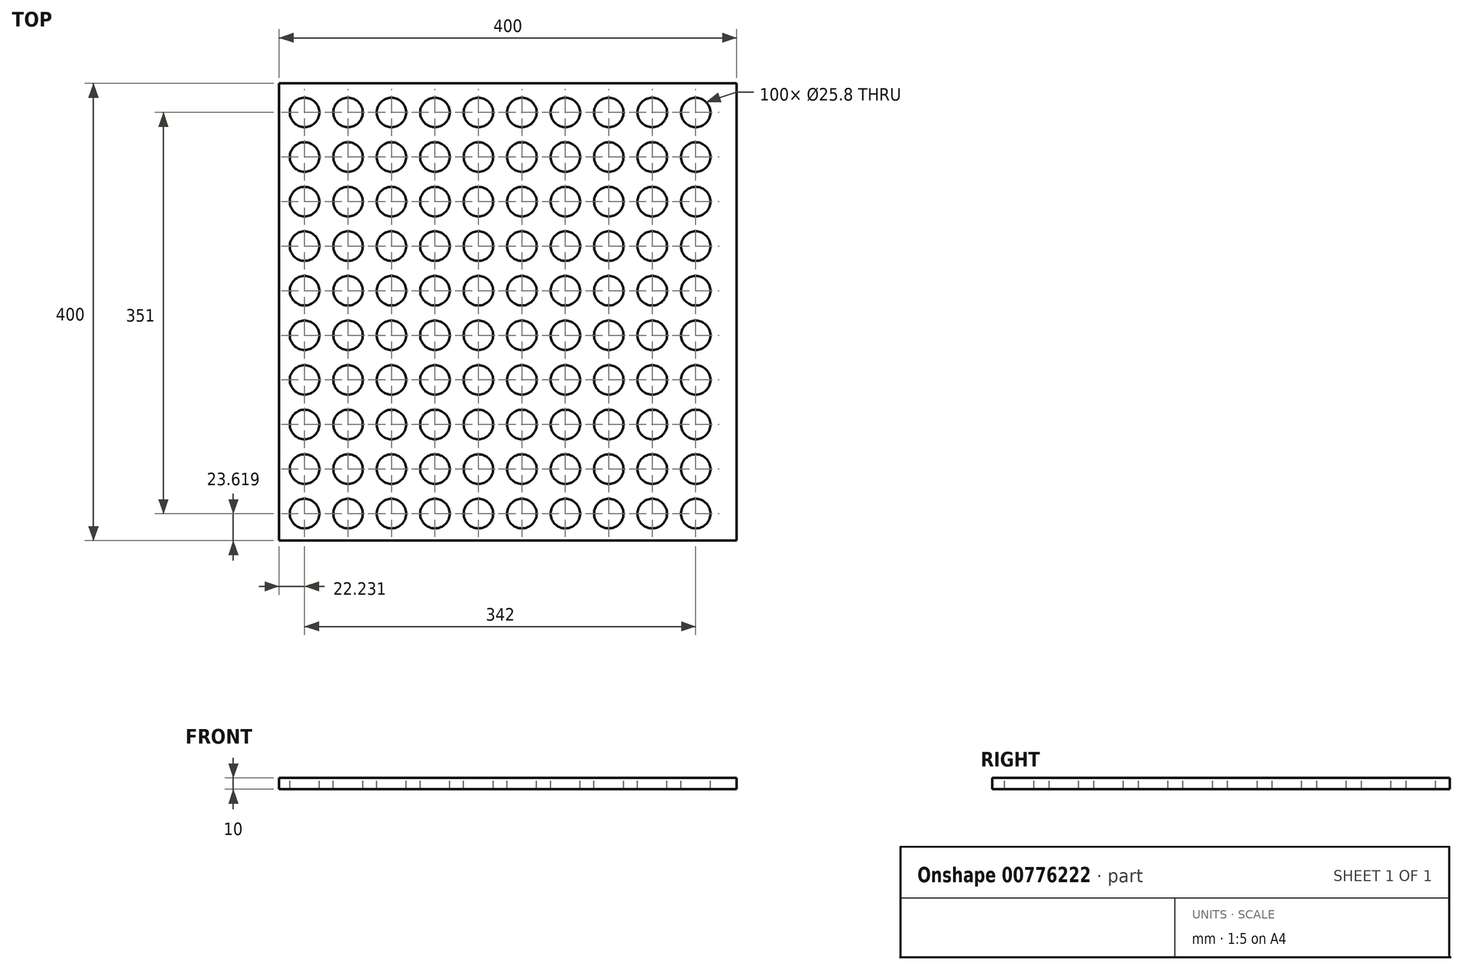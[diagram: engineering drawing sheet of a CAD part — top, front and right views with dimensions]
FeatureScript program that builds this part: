
annotation { "Feature Type Name" : "Feature", "Feature Type Description" : "" }
export const myFeature = defineFeature(function(context is Context, id is Id, definition is map)
    precondition{}
    {
        {
            var Q0;
            Q0=qCreatedBy(makeId("Top.planeOp"),FACE);
            var sketch = newSketch(context, id + "F0", { "sketchPlane" : qUnion([Q0])});
            skLineSegment(sketch, "E0.bottom", {"start": v(-200, 200) * mm, "end": v(200, 200) * mm});
            skLineSegment(sketch, "E0.top", {"start": v(-200, -200) * mm, "end": v(200, -200) * mm});
            skLineSegment(sketch, "E0.left", {"start": v(-200, 200) * mm, "end": v(-200, -200) * mm});
            skLineSegment(sketch, "E0.right", {"start": v(200, 200) * mm, "end": v(200, -200) * mm});
            skPoint(sketch, "E0.middle", {"position": v(0, 0) * mm});
            skSolve(sketch);
        }
        {
            var Q0;
            Q0=qSketchRegion(id+"F0",true);
            extrude(context, id + "F1", {"entities" : qUnion([Q0]), "depth" : 10 * mm, "offsetDistance" : 25 * mm});
        }
        {
            var Q0;
            Q0=makeQuery(id+"F1.opExtrude","CAP_FACE",FACE,{"disambiguationData":[OSD([sQuery(id+"F0.wireOp",EDGE,"E0.bottom"),sQuery(id+"F0.wireOp",EDGE,"E0.top"),sQuery(id+"F0.wireOp",EDGE,"E0.left"),sQuery(id+"F0.wireOp",EDGE,"E0.right")])],"isStart":false});
            var sketch = newSketch(context, id + "F2", { "sketchPlane" : qUnion([Q0])});
            skCircle(sketch, "E1", {"center": v(164.23, -176.38) * mm, "radius": 12.9 * mm});
            skCircle(sketch, "E2.0.1.0", {"center": v(164.23, -137.38) * mm, "radius": 12.9 * mm});
            skCircle(sketch, "E2.0.2.0", {"center": v(164.23, -98.38) * mm, "radius": 12.9 * mm});
            skCircle(sketch, "E2.0.3.0", {"center": v(164.23, -59.38) * mm, "radius": 12.9 * mm});
            skCircle(sketch, "E2.0.4.0", {"center": v(164.23, -20.38) * mm, "radius": 12.9 * mm});
            skCircle(sketch, "E2.0.5.0", {"center": v(164.23, 18.62) * mm, "radius": 12.9 * mm});
            skCircle(sketch, "E2.0.6.0", {"center": v(164.23, 57.62) * mm, "radius": 12.9 * mm});
            skCircle(sketch, "E2.0.7.0", {"center": v(164.23, 96.62) * mm, "radius": 12.9 * mm});
            skCircle(sketch, "E2.0.8.0", {"center": v(164.23, 135.62) * mm, "radius": 12.9 * mm});
            skCircle(sketch, "E2.0.9.0", {"center": v(164.23, 174.62) * mm, "radius": 12.9 * mm});
            skCircle(sketch, "E2.1.0.0", {"center": v(126.23, -176.38) * mm, "radius": 12.9 * mm});
            skCircle(sketch, "E2.1.1.0", {"center": v(126.23, -137.38) * mm, "radius": 12.9 * mm});
            skCircle(sketch, "E2.1.2.0", {"center": v(126.23, -98.38) * mm, "radius": 12.9 * mm});
            skCircle(sketch, "E2.1.3.0", {"center": v(126.23, -59.38) * mm, "radius": 12.9 * mm});
            skCircle(sketch, "E2.1.4.0", {"center": v(126.23, -20.38) * mm, "radius": 12.9 * mm});
            skCircle(sketch, "E2.1.5.0", {"center": v(126.23, 18.62) * mm, "radius": 12.9 * mm});
            skCircle(sketch, "E2.1.6.0", {"center": v(126.23, 57.62) * mm, "radius": 12.9 * mm});
            skCircle(sketch, "E2.1.7.0", {"center": v(126.23, 96.62) * mm, "radius": 12.9 * mm});
            skCircle(sketch, "E2.1.8.0", {"center": v(126.23, 135.62) * mm, "radius": 12.9 * mm});
            skCircle(sketch, "E2.1.9.0", {"center": v(126.23, 174.62) * mm, "radius": 12.9 * mm});
            skCircle(sketch, "E2.2.0.0", {"center": v(88.23, -176.38) * mm, "radius": 12.9 * mm});
            skCircle(sketch, "E2.2.1.0", {"center": v(88.23, -137.38) * mm, "radius": 12.9 * mm});
            skCircle(sketch, "E2.2.2.0", {"center": v(88.23, -98.38) * mm, "radius": 12.9 * mm});
            skCircle(sketch, "E2.2.3.0", {"center": v(88.23, -59.38) * mm, "radius": 12.9 * mm});
            skCircle(sketch, "E2.2.4.0", {"center": v(88.23, -20.38) * mm, "radius": 12.9 * mm});
            skCircle(sketch, "E2.2.5.0", {"center": v(88.23, 18.62) * mm, "radius": 12.9 * mm});
            skCircle(sketch, "E2.2.6.0", {"center": v(88.23, 57.62) * mm, "radius": 12.9 * mm});
            skCircle(sketch, "E2.2.7.0", {"center": v(88.23, 96.62) * mm, "radius": 12.9 * mm});
            skCircle(sketch, "E2.2.8.0", {"center": v(88.23, 135.62) * mm, "radius": 12.9 * mm});
            skCircle(sketch, "E2.2.9.0", {"center": v(88.23, 174.62) * mm, "radius": 12.9 * mm});
            skCircle(sketch, "E2.3.0.0", {"center": v(50.23, -176.38) * mm, "radius": 12.9 * mm});
            skCircle(sketch, "E2.3.1.0", {"center": v(50.23, -137.38) * mm, "radius": 12.9 * mm});
            skCircle(sketch, "E2.3.2.0", {"center": v(50.23, -98.38) * mm, "radius": 12.9 * mm});
            skCircle(sketch, "E2.3.3.0", {"center": v(50.23, -59.38) * mm, "radius": 12.9 * mm});
            skCircle(sketch, "E2.3.4.0", {"center": v(50.23, -20.38) * mm, "radius": 12.9 * mm});
            skCircle(sketch, "E2.3.5.0", {"center": v(50.23, 18.62) * mm, "radius": 12.9 * mm});
            skCircle(sketch, "E2.3.6.0", {"center": v(50.23, 57.62) * mm, "radius": 12.9 * mm});
            skCircle(sketch, "E2.3.7.0", {"center": v(50.23, 96.62) * mm, "radius": 12.9 * mm});
            skCircle(sketch, "E2.3.8.0", {"center": v(50.23, 135.62) * mm, "radius": 12.9 * mm});
            skCircle(sketch, "E2.3.9.0", {"center": v(50.23, 174.62) * mm, "radius": 12.9 * mm});
            skCircle(sketch, "E2.4.0.0", {"center": v(12.23, -176.38) * mm, "radius": 12.9 * mm});
            skCircle(sketch, "E2.4.1.0", {"center": v(12.23, -137.38) * mm, "radius": 12.9 * mm});
            skCircle(sketch, "E2.4.2.0", {"center": v(12.23, -98.38) * mm, "radius": 12.9 * mm});
            skCircle(sketch, "E2.4.3.0", {"center": v(12.23, -59.38) * mm, "radius": 12.9 * mm});
            skCircle(sketch, "E2.4.4.0", {"center": v(12.23, -20.38) * mm, "radius": 12.9 * mm});
            skCircle(sketch, "E2.4.5.0", {"center": v(12.23, 18.62) * mm, "radius": 12.9 * mm});
            skCircle(sketch, "E2.4.6.0", {"center": v(12.23, 57.62) * mm, "radius": 12.9 * mm});
            skCircle(sketch, "E2.4.7.0", {"center": v(12.23, 96.62) * mm, "radius": 12.9 * mm});
            skCircle(sketch, "E2.4.8.0", {"center": v(12.23, 135.62) * mm, "radius": 12.9 * mm});
            skCircle(sketch, "E2.4.9.0", {"center": v(12.23, 174.62) * mm, "radius": 12.9 * mm});
            skCircle(sketch, "E2.5.0.0", {"center": v(-25.77, -176.38) * mm, "radius": 12.9 * mm});
            skCircle(sketch, "E2.5.1.0", {"center": v(-25.77, -137.38) * mm, "radius": 12.9 * mm});
            skCircle(sketch, "E2.5.2.0", {"center": v(-25.77, -98.38) * mm, "radius": 12.9 * mm});
            skCircle(sketch, "E2.5.3.0", {"center": v(-25.77, -59.38) * mm, "radius": 12.9 * mm});
            skCircle(sketch, "E2.5.4.0", {"center": v(-25.77, -20.38) * mm, "radius": 12.9 * mm});
            skCircle(sketch, "E2.5.5.0", {"center": v(-25.77, 18.62) * mm, "radius": 12.9 * mm});
            skCircle(sketch, "E2.5.6.0", {"center": v(-25.77, 57.62) * mm, "radius": 12.9 * mm});
            skCircle(sketch, "E2.5.7.0", {"center": v(-25.77, 96.62) * mm, "radius": 12.9 * mm});
            skCircle(sketch, "E2.5.8.0", {"center": v(-25.77, 135.62) * mm, "radius": 12.9 * mm});
            skCircle(sketch, "E2.5.9.0", {"center": v(-25.77, 174.62) * mm, "radius": 12.9 * mm});
            skCircle(sketch, "E2.6.0.0", {"center": v(-63.77, -176.38) * mm, "radius": 12.9 * mm});
            skCircle(sketch, "E2.6.1.0", {"center": v(-63.77, -137.38) * mm, "radius": 12.9 * mm});
            skCircle(sketch, "E2.6.2.0", {"center": v(-63.77, -98.38) * mm, "radius": 12.9 * mm});
            skCircle(sketch, "E2.6.3.0", {"center": v(-63.77, -59.38) * mm, "radius": 12.9 * mm});
            skCircle(sketch, "E2.6.4.0", {"center": v(-63.77, -20.38) * mm, "radius": 12.9 * mm});
            skCircle(sketch, "E2.6.5.0", {"center": v(-63.77, 18.62) * mm, "radius": 12.9 * mm});
            skCircle(sketch, "E2.6.6.0", {"center": v(-63.77, 57.62) * mm, "radius": 12.9 * mm});
            skCircle(sketch, "E2.6.7.0", {"center": v(-63.77, 96.62) * mm, "radius": 12.9 * mm});
            skCircle(sketch, "E2.6.8.0", {"center": v(-63.77, 135.62) * mm, "radius": 12.9 * mm});
            skCircle(sketch, "E2.6.9.0", {"center": v(-63.77, 174.62) * mm, "radius": 12.9 * mm});
            skCircle(sketch, "E2.7.0.0", {"center": v(-101.77, -176.38) * mm, "radius": 12.9 * mm});
            skCircle(sketch, "E2.7.1.0", {"center": v(-101.77, -137.38) * mm, "radius": 12.9 * mm});
            skCircle(sketch, "E2.7.2.0", {"center": v(-101.77, -98.38) * mm, "radius": 12.9 * mm});
            skCircle(sketch, "E2.7.3.0", {"center": v(-101.77, -59.38) * mm, "radius": 12.9 * mm});
            skCircle(sketch, "E2.7.4.0", {"center": v(-101.77, -20.38) * mm, "radius": 12.9 * mm});
            skCircle(sketch, "E2.7.5.0", {"center": v(-101.77, 18.62) * mm, "radius": 12.9 * mm});
            skCircle(sketch, "E2.7.6.0", {"center": v(-101.77, 57.62) * mm, "radius": 12.9 * mm});
            skCircle(sketch, "E2.7.7.0", {"center": v(-101.77, 96.62) * mm, "radius": 12.9 * mm});
            skCircle(sketch, "E2.7.8.0", {"center": v(-101.77, 135.62) * mm, "radius": 12.9 * mm});
            skCircle(sketch, "E2.7.9.0", {"center": v(-101.77, 174.62) * mm, "radius": 12.9 * mm});
            skCircle(sketch, "E2.8.0.0", {"center": v(-139.77, -176.38) * mm, "radius": 12.9 * mm});
            skCircle(sketch, "E2.8.1.0", {"center": v(-139.77, -137.38) * mm, "radius": 12.9 * mm});
            skCircle(sketch, "E2.8.2.0", {"center": v(-139.77, -98.38) * mm, "radius": 12.9 * mm});
            skCircle(sketch, "E2.8.3.0", {"center": v(-139.77, -59.38) * mm, "radius": 12.9 * mm});
            skCircle(sketch, "E2.8.4.0", {"center": v(-139.77, -20.38) * mm, "radius": 12.9 * mm});
            skCircle(sketch, "E2.8.5.0", {"center": v(-139.77, 18.62) * mm, "radius": 12.9 * mm});
            skCircle(sketch, "E2.8.6.0", {"center": v(-139.77, 57.62) * mm, "radius": 12.9 * mm});
            skCircle(sketch, "E2.8.7.0", {"center": v(-139.77, 96.62) * mm, "radius": 12.9 * mm});
            skCircle(sketch, "E2.8.8.0", {"center": v(-139.77, 135.62) * mm, "radius": 12.9 * mm});
            skCircle(sketch, "E2.8.9.0", {"center": v(-139.77, 174.62) * mm, "radius": 12.9 * mm});
            skCircle(sketch, "E2.9.0.0", {"center": v(-177.77, -176.38) * mm, "radius": 12.9 * mm});
            skCircle(sketch, "E2.9.1.0", {"center": v(-177.77, -137.38) * mm, "radius": 12.9 * mm});
            skCircle(sketch, "E2.9.2.0", {"center": v(-177.77, -98.38) * mm, "radius": 12.9 * mm});
            skCircle(sketch, "E2.9.3.0", {"center": v(-177.77, -59.38) * mm, "radius": 12.9 * mm});
            skCircle(sketch, "E2.9.4.0", {"center": v(-177.77, -20.38) * mm, "radius": 12.9 * mm});
            skCircle(sketch, "E2.9.5.0", {"center": v(-177.77, 18.62) * mm, "radius": 12.9 * mm});
            skCircle(sketch, "E2.9.6.0", {"center": v(-177.77, 57.62) * mm, "radius": 12.9 * mm});
            skCircle(sketch, "E2.9.7.0", {"center": v(-177.77, 96.62) * mm, "radius": 12.9 * mm});
            skCircle(sketch, "E2.9.8.0", {"center": v(-177.77, 135.62) * mm, "radius": 12.9 * mm});
            skCircle(sketch, "E2.9.9.0", {"center": v(-177.77, 174.62) * mm, "radius": 12.9 * mm});
            skLineSegment(sketch, "E2.direction1", {"start": v(164.23, -176.38) * mm, "end": v(126.23, -176.38) * mm, "construction": true});
            skLineSegment(sketch, "E2.direction2", {"start": v(164.23, -176.38) * mm, "end": v(164.23, -137.38) * mm, "construction": true});
            skSolve(sketch);
        }
        {
            var Q0;
            Q0=qSketchRegion(id+"F2",true);
            extrude(context, id + "F3", {"entities" : qUnion([Q0]), "operationType" : NewBodyOperationType.REMOVE, "oppositeDirection" : true, "depth" : 13 * mm, "offsetDistance" : 25 * mm});
        }
    });
